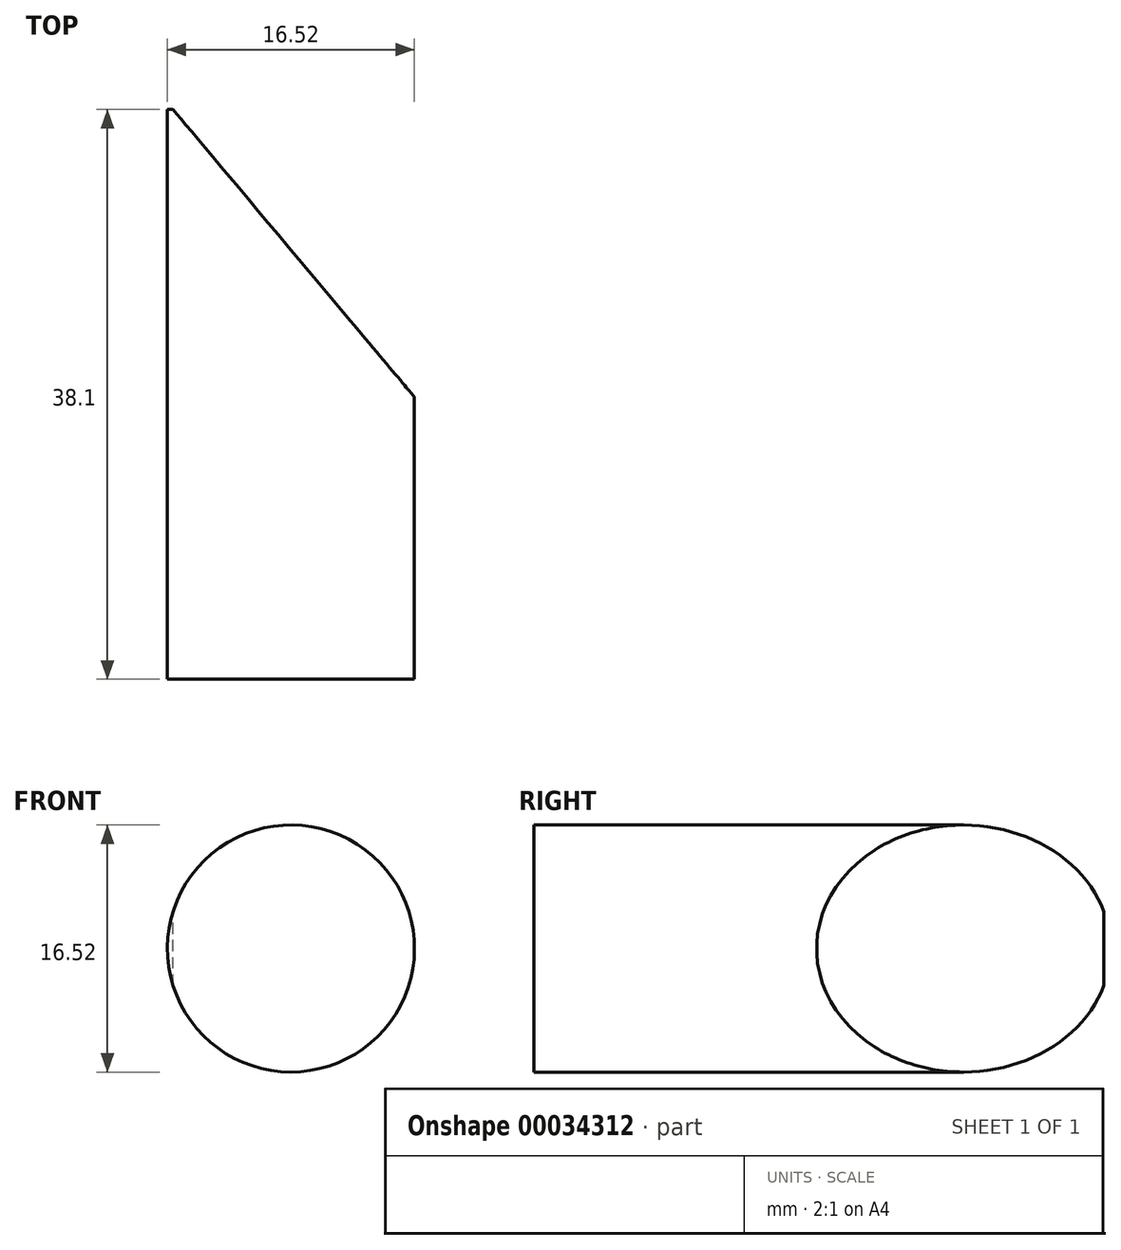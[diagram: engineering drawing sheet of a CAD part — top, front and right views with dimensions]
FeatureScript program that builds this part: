
annotation { "Feature Type Name" : "Feature", "Feature Type Description" : "" }
export const myFeature = defineFeature(function(context is Context, id is Id, definition is map)
    precondition{}
    {
        {
            var Q0;
            Q0=qCreatedBy(makeId("Front.planeOp"),FACE);
            var sketch = newSketch(context, id + "F0", { "sketchPlane" : qUnion([Q0])});
            skCircle(sketch, "E0", {"center": v(0, 0) * mm, "radius": 8.26 * mm});
            skSolve(sketch);
        }
        {
            var Q0;
            Q0=makeQuery(id+"F0.imprint","IMPRINT",FACE,{"disambiguationData":[TD([[makeQuery(id+"F0.imprint","IMPRINT",EDGE,{"derivedFrom":sQuery(id+"F0.wireOp",EDGE,"E0")}),1.0]])]});
            extrude(context, id + "F1", {"entities" : qUnion([Q0]), "depth" : 38.1 * mm});
        }
        {
            var Q0;
            Q0=qCreatedBy(makeId("Top.planeOp"),FACE);
            var sketch = newSketch(context, id + "F2", { "sketchPlane" : qUnion([Q0])});
            skLineSegment(sketch, "E1", {"start": v(-7.88, 0) * mm, "end": v(4.97, -15.32) * mm});
            skLineSegment(sketch, "E2", {"start": v(4.97, -15.32) * mm, "end": v(4.97, 0) * mm});
            skLineSegment(sketch, "E3", {"start": v(4.97, 0) * mm, "end": v(-7.88, 0) * mm});
            skLineSegment(sketch, "E4", {"start": v(4.97, -15.32) * mm, "end": v(9.58, -20.8) * mm});
            skLineSegment(sketch, "E5", {"start": v(9.58, -20.8) * mm, "end": v(9.58, 0) * mm});
            skLineSegment(sketch, "E6", {"start": v(9.58, 0) * mm, "end": v(-7.88, 0) * mm});
            skSolve(sketch);
        }
        {
            var Q0;
            Q0 = qSketchRegion(id + "F2", true);
            extrude(context, id + "F3", {"entities" : qUnion([Q0]), "operationType" : NewBodyOperationType.REMOVE, "oppositeDirection" : true, "depth" : 56.63 * mm});
        }
        {
            var Q0;
            Q0=makeQuery(id+"F3.boolean.opBoolean","COPY",FACE,{"derivedFrom":makeQuery(id+"F3.opExtrude","CAP_FACE",FACE,{"disambiguationData":[OSD([sQuery(id+"F2.wireOp",EDGE,"E1"),sQuery(id+"F2.wireOp",EDGE,"E4"),sQuery(id+"F2.wireOp",EDGE,"E5"),sQuery(id+"F2.wireOp",EDGE,"E6")])],"isStart":true})});
            extrude(context, id + "F4", {"entities" : qUnion([Q0]), "operationType" : NewBodyOperationType.REMOVE, "oppositeDirection" : true, "depth" : 25.4 * mm});
        }
    });
